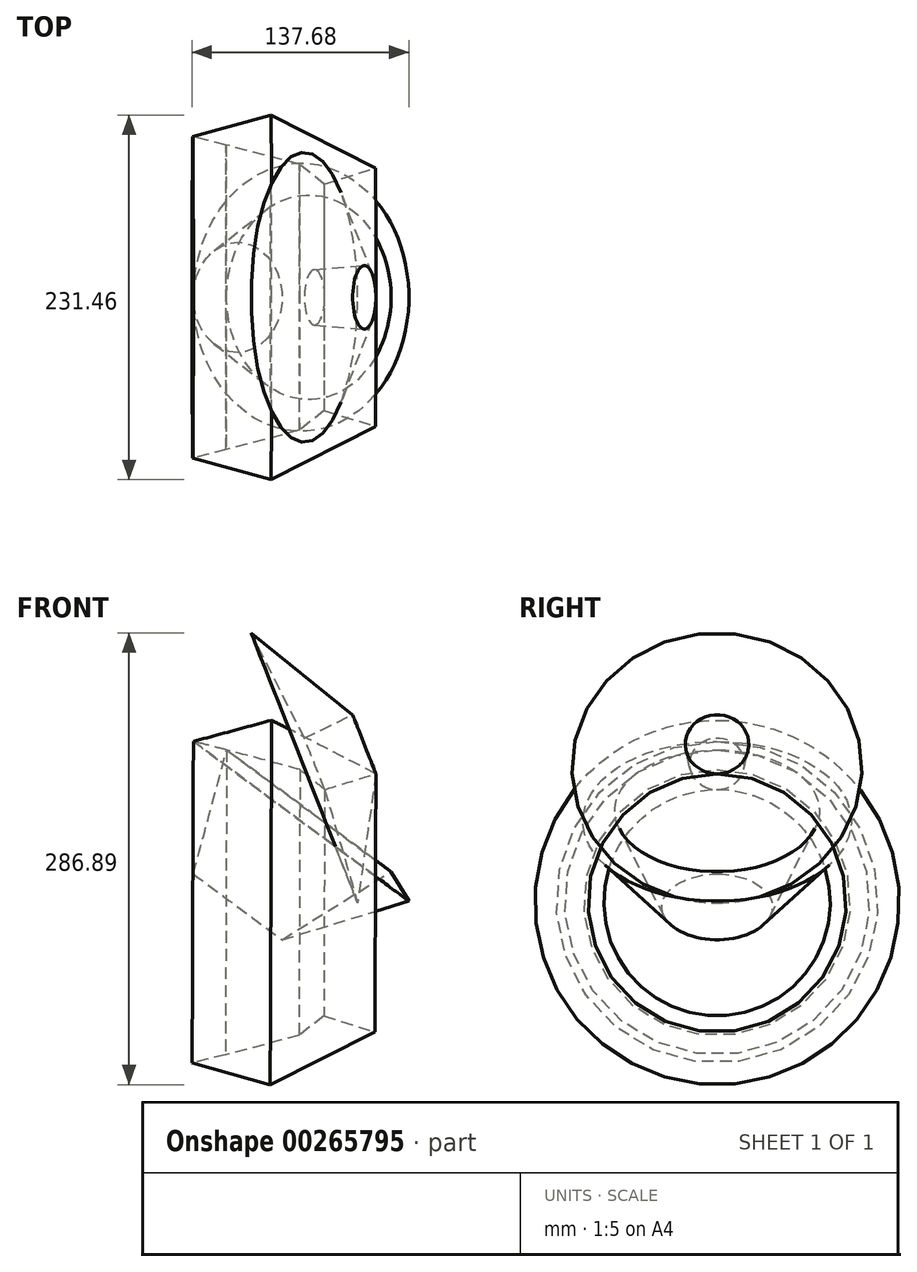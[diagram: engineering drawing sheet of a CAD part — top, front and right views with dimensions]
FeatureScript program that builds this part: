
annotation { "Feature Type Name" : "Feature", "Feature Type Description" : "" }
export const myFeature = defineFeature(function(context is Context, id is Id, definition is map)
    precondition{}
    {
        {
            var Q0;
            Q0=qCreatedBy(makeId("Front.planeOp"),FACE);
            var sketch = newSketch(context, id + "F0", { "sketchPlane" : qUnion([Q0])});
            skLineSegment(sketch, "E0", {"start": v(-39.98, 22.85) * mm, "end": v(-29.41, -42.55) * mm});
            skLineSegment(sketch, "E1", {"start": v(-29.41, -42.55) * mm, "end": v(23.7, 29.13) * mm});
            skLineSegment(sketch, "E2", {"start": v(23.7, 29.13) * mm, "end": v(44.55, -42.84) * mm});
            skLineSegment(sketch, "E3", {"start": v(44.55, -42.84) * mm, "end": v(56.26, 39.12) * mm});
            skLineSegment(sketch, "E4", {"start": v(56.26, 39.12) * mm, "end": v(-10, 73.1) * mm});
            skLineSegment(sketch, "E5", {"start": v(-10, 73.1) * mm, "end": v(-59.68, 59.68) * mm});
            skLineSegment(sketch, "E6", {"start": v(-59.68, 59.68) * mm, "end": v(-59.68, -24.56) * mm});
            skLineSegment(sketch, "E7", {"start": v(-59.68, -24.56) * mm, "end": v(-38.55, 54.26) * mm});
            skLineSegment(sketch, "E8", {"start": v(-38.55, 54.26) * mm, "end": v(8.02, 41.77) * mm});
            skLineSegment(sketch, "E9", {"start": v(8.02, 41.77) * mm, "end": v(-39.98, 22.85) * mm});
            skLineSegment(sketch, "E10", {"start": v(8.02, 41.77) * mm, "end": v(23.7, 29.13) * mm});
            skLineSegment(sketch, "E11", {"start": v(-38.55, 54.26) * mm, "end": v(-59.68, 59.68) * mm});
            skLineSegment(sketch, "E12", {"start": v(23.7, 29.13) * mm, "end": v(56.26, 39.12) * mm});
            skLineSegment(sketch, "E13", {"start": v(-29.41, -42.55) * mm, "end": v(-59.68, -24.56) * mm});
            skLineSegment(sketch, "E14", {"start": v(-29.41, -42.55) * mm, "end": v(44.55, -42.84) * mm});
            skSolve(sketch);
        }
        {
            var Q0;
            Q0=makeQuery(id+"F0.imprint","IMPRINT",FACE,{"disambiguationData":[TD([[makeQuery(id+"F0.imprint","IMPRINT",EDGE,{"derivedFrom":sQuery(id+"F0.wireOp",EDGE,"E4")}),1.0]])]});
            var Q1;
            Q1=sQuery(id+"F0.wireOp",EDGE,"E14");
            revolve(context, id + "F1", {"entities" : qUnion([Q0]), "axis" : qUnion([Q1]), "revolveType" : RevolveType.FULL});
        }
        {
            var Q0;
            Q0=makeQuery(id+"F0.imprint","IMPRINT",FACE,{"disambiguationData":[TD([[makeQuery(id+"F0.imprint","IMPRINT",EDGE,{"derivedFrom":sQuery(id+"F0.wireOp",EDGE,"E2")}),1.0]])]});
            var Q1;
            Q1=sQuery(id+"F0.wireOp",EDGE,"E9");
            revolve(context, id + "F2", {"entities" : qUnion([Q0]), "axis" : qUnion([Q1]), "revolveType" : RevolveType.FULL});
        }
        {
            var Q0;
            Q0=makeQuery(id+"F0.imprint","IMPRINT",FACE,{"disambiguationData":[TD([[makeQuery(id+"F0.imprint","IMPRINT",EDGE,{"derivedFrom":sQuery(id+"F0.wireOp",EDGE,"E6")}),1.0]])]});
            var Q1;
            Q1=sQuery(id+"F0.wireOp",EDGE,"E1");
            revolve(context, id + "F3", {"entities" : qUnion([Q0]), "axis" : qUnion([Q1]), "revolveType" : RevolveType.FULL});
        }
    });
